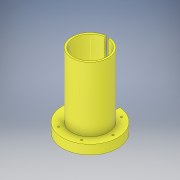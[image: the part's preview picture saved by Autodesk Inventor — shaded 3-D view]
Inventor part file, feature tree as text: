
AUTODESK INVENTOR PART (.ipt)
format: ipt  version: 2019.3 (Build 233278000, 278)  size: 154,624 bytes
history: native  units: in
note: dims shown in document units (in); Inventor stores cm internally (conversion verified against a paired STEP export)
features: sketch x2, revolve x1, extrude x1, hole x1, pattern_circular x1
ambient origin geometry x8: Origin, YZ Plane, XZ Plane, XY Plane, X Axis, Y Axis, Z Axis, Center Point
bodies: Solid2 (feature_tree)
feature tree (6):
  revolve  "Revolution3"  [1 undecoded]
  extrude  "Extrusion5"  TaperAngle=90.0deg  [1 undecoded]
  hole  "Hole4"  [1 undecoded]
  pattern_circular  "Circular Pattern2"  [2 undecoded]
  sketch  "Sketch13"  dims[d49=0.5in d50=4.0in]
  sketch  "Sketch17"  dims[d53=0.1in d55=90.0deg d56=0.0378in d57=0.0378in d58=1.0in d59=0.0in d60=0.5in d72=0.895in d73=1.25in d74=0.104in d75=0.276in d76=0.185in d77=0.281in d78=0.5635in d79=1.0in d80=0.8108in d81=2.3622in d82=360.0deg]
note: 5 required parameter values undecoded (feature->parameter linkage not recoverable at this tier; creation-order binding heuristic only, values carry confidence <= 0.55)